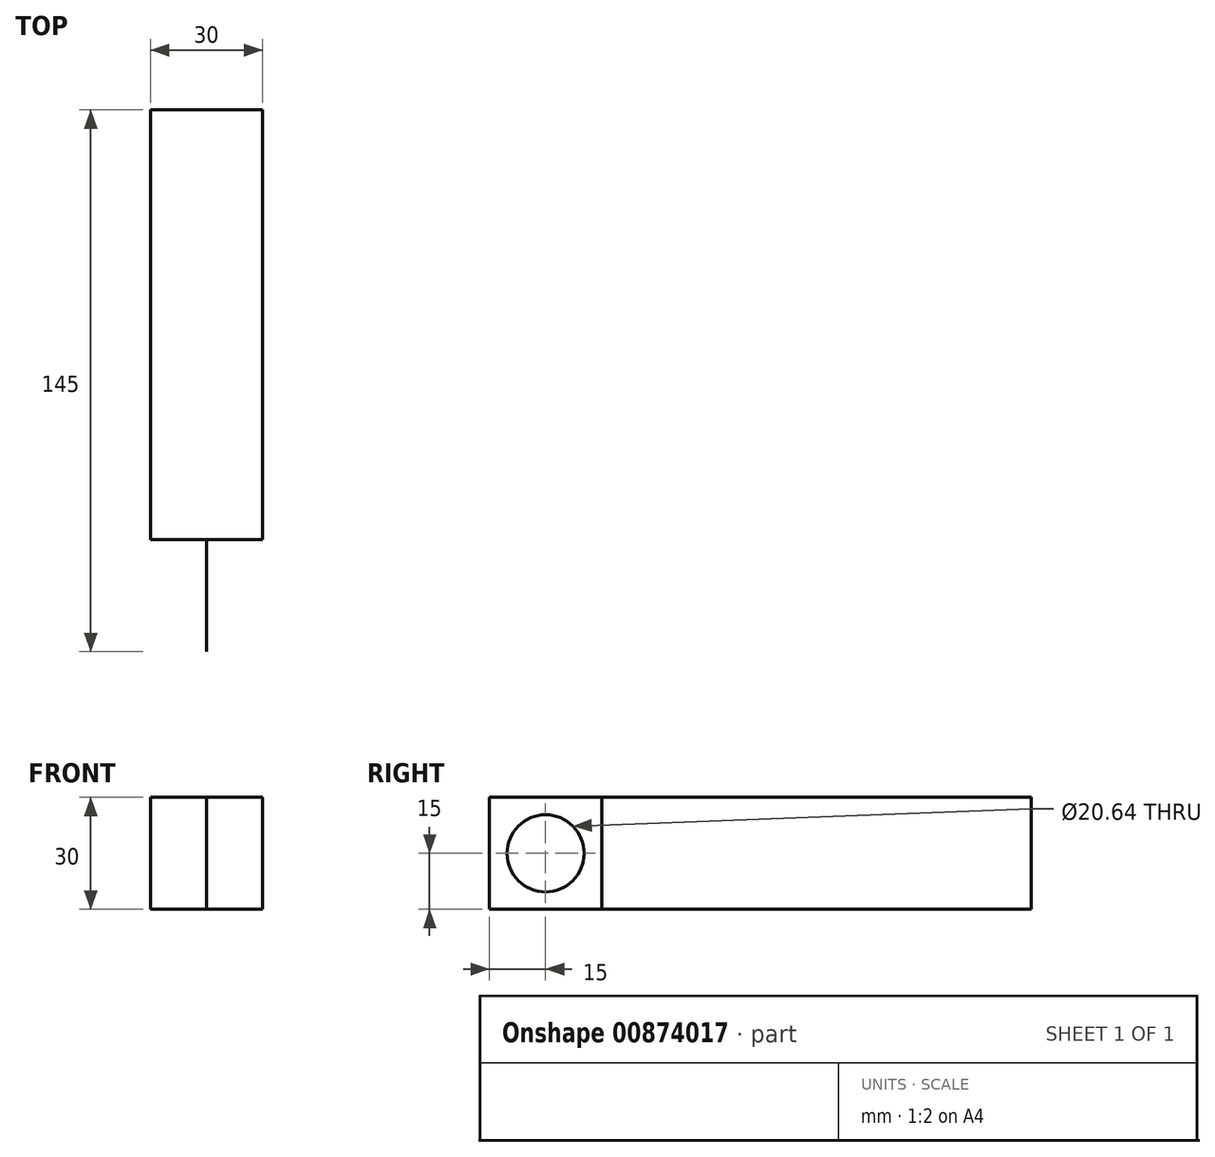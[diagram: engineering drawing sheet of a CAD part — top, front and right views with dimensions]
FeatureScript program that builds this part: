
annotation { "Feature Type Name" : "Feature", "Feature Type Description" : "" }
export const myFeature = defineFeature(function(context is Context, id is Id, definition is map)
    precondition{}
    {
        {
            var Q0;
            Q0=qCreatedBy(makeId("Right.planeOp"),FACE);
            var sketch = newSketch(context, id + "F0", { "sketchPlane" : qUnion([Q0])});
            skLineSegment(sketch, "E0.bottom", {"start": v(15, -15) * mm, "end": v(-15, -15) * mm});
            skLineSegment(sketch, "E0.top", {"start": v(15, 15) * mm, "end": v(-15, 15) * mm});
            skLineSegment(sketch, "E0.left", {"start": v(15, -15) * mm, "end": v(15, 15) * mm});
            skLineSegment(sketch, "E0.right", {"start": v(-15, -15) * mm, "end": v(-15, 15) * mm});
            skPoint(sketch, "E0.middle", {"position": v(0, 0) * mm});
            skCircle(sketch, "E1", {"center": v(0, 0) * mm, "radius": 10.32 * mm});
            skLineSegment(sketch, "E2.bottom", {"start": v(15, -15) * mm, "end": v(130, -15) * mm});
            skLineSegment(sketch, "E2.top", {"start": v(15, 15) * mm, "end": v(130, 15) * mm});
            skLineSegment(sketch, "E2.right", {"start": v(130, -15) * mm, "end": v(130, 15) * mm});
            skSolve(sketch);
        }
        {
            var Q0;
            Q0=makeQuery(id+"F0.imprint","IMPRINT",FACE,{"disambiguationData":[TD([[makeQuery(id+"F0.imprint","IMPRINT",EDGE,{"derivedFrom":sQuery(id+"F0.wireOp",EDGE,"E0.bottom")}),-1.0]])]});
            extrude(context, id + "F1", {"entities" : qUnion([Q0]), "endBound" : BoundingType.SYMMETRIC, "depth" : 5 / 406.4 * mm, "offsetDistance" : 25 * mm});
        }
        {
            var Q0;
            Q0=makeQuery(id+"F0.imprint","IMPRINT",FACE,{"disambiguationData":[TD([[makeQuery(id+"F0.imprint","IMPRINT",EDGE,{"derivedFrom":sQuery(id+"F0.wireOp",EDGE,"E2.bottom")}),1.0]])]});
            extrude(context, id + "F2", {"entities" : qUnion([Q0]), "operationType" : NewBodyOperationType.ADD, "endBound" : BoundingType.SYMMETRIC, "depth" : 30 * mm, "offsetDistance" : 25 * mm});
        }
    });
